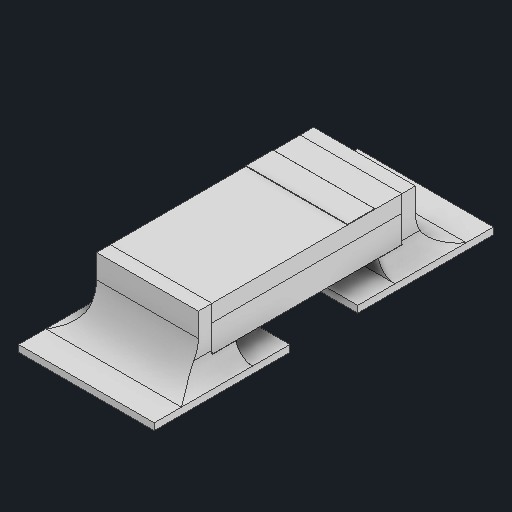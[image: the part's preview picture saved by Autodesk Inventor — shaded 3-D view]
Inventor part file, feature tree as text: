
AUTODESK INVENTOR PART (.ipt)
format: ipt  version: 2023 (Build 270158000, 158)  size: 131,072 bytes
history: native  units: in
note: dims shown in document units (in); Inventor stores cm internally (conversion verified against a paired STEP export)
features: other x3, fillet x2
ambient origin geometry x8: Origin, YZ Plane, XZ Plane, XY Plane, X Axis, Y Axis, Z Axis, Center Point
bodies: Solid1 (feature_tree), Solid2 (feature_tree), Solid3 (feature_tree), Solid4 (feature_tree), Solid5 (feature_tree)
feature tree (5):
  other  "Boss-Extrude1"
  fillet  "Fillet4"  [1 undecoded]
  fillet  "Fillet3"  [1 undecoded]
  other  "Boss-Extrude4"
  other  "Boss-Extrude5"
note: 2 required parameter values undecoded (feature->parameter linkage not recoverable at this tier; creation-order binding heuristic only, values carry confidence <= 0.55)
